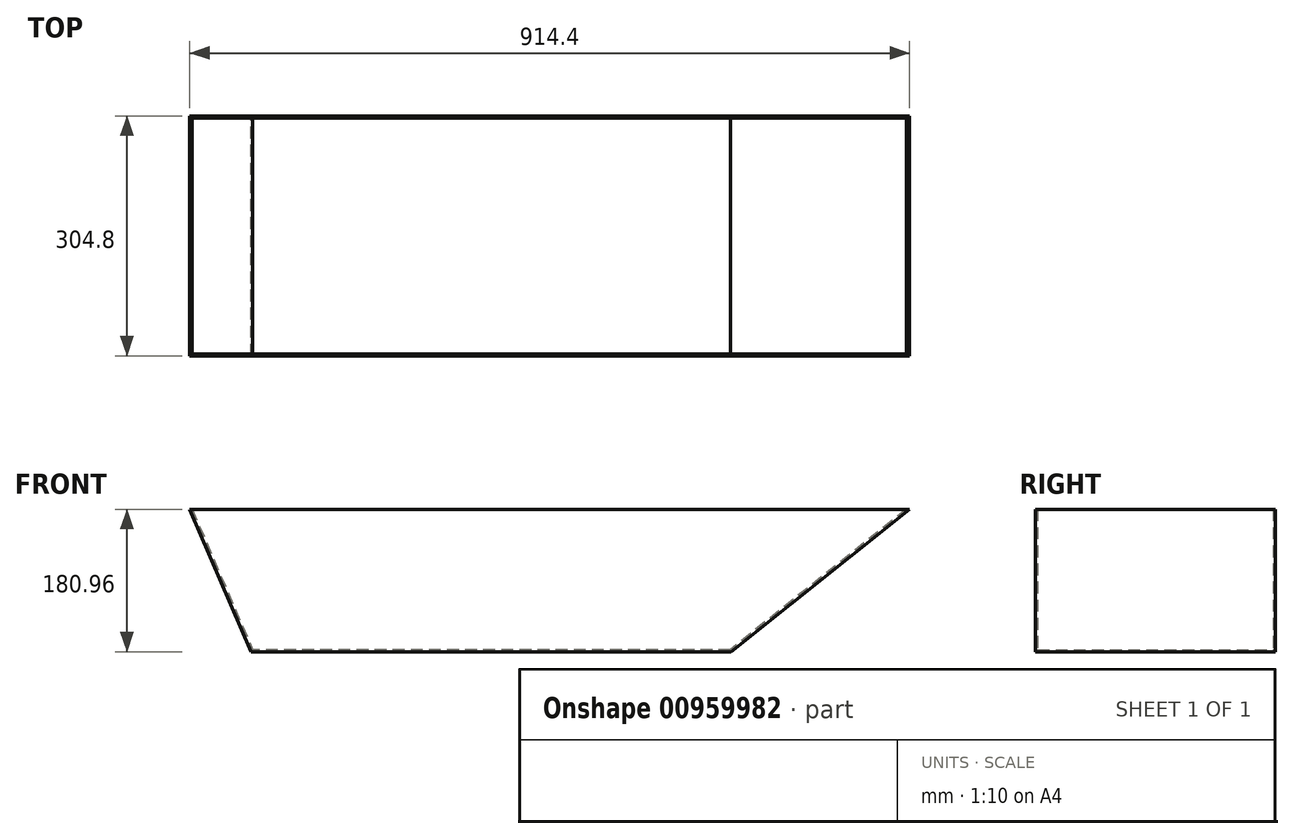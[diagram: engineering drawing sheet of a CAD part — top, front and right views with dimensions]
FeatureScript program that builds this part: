
annotation { "Feature Type Name" : "Feature", "Feature Type Description" : "" }
export const myFeature = defineFeature(function(context is Context, id is Id, definition is map)
    precondition{}
    {
        {
            var Q0;
            Q0=qCreatedBy(makeId("Front.planeOp"),FACE);
            var sketch = newSketch(context, id + "F0", { "sketchPlane" : qUnion([Q0])});
            skLineSegment(sketch, "E0", {"start": v(535.52, 0) * mm, "end": v(-378.88, 0) * mm});
            skLineSegment(sketch, "E1", {"start": v(308.76, -180.96) * mm, "end": v(-300.84, -180.96) * mm});
            skLineSegment(sketch, "E2", {"start": v(-378.88, 0) * mm, "end": v(-300.84, -180.96) * mm});
            skLineSegment(sketch, "E3", {"start": v(535.52, 0) * mm, "end": v(308.76, -180.96) * mm});
            skSolve(sketch);
        }
        {
            var Q0;
            Q0=makeQuery(id+"F0.imprint","IMPRINT",FACE,{"disambiguationData":[TD([[makeQuery(id+"F0.imprint","IMPRINT",EDGE,{"derivedFrom":sQuery(id+"F0.wireOp",EDGE,"E0")}),1.0]])]});
            var sketch = newSketch(context, id + "F1", { "sketchPlane" : qUnion([Q0])});
            skSolve(sketch);
        }
        {
            var Q0;
            Q0=makeQuery(id+"F1.imprint","IMPRINT",FACE,{"disambiguationData":[TD([[makeQuery(id+"F1.imprint","IMPRINT",EDGE,{"derivedFrom":makeQuery(id+"F0.imprint","IMPRINT",EDGE,{"derivedFrom":sQuery(id+"F0.wireOp",EDGE,"E0")})}),1.0]])]});
            extrude(context, id + "F2", {"entities" : qUnion([Q0]), "endBound" : BoundingType.SYMMETRIC, "depth" : 304.8 * mm, "offsetDistance" : 25.4 * mm});
        }
        {
            var Q0;
            Q0=makeQuery(id+"F2.opExtrude","SWEPT_FACE",FACE,{"disambiguationData":[OSD([sQuery(id+"F0.wireOp",EDGE,"E0")])]});
            shell(context, id + "F3", {"entities" : qUnion([Q0]), "thickness" : 2.54 * mm});
        }
    });
